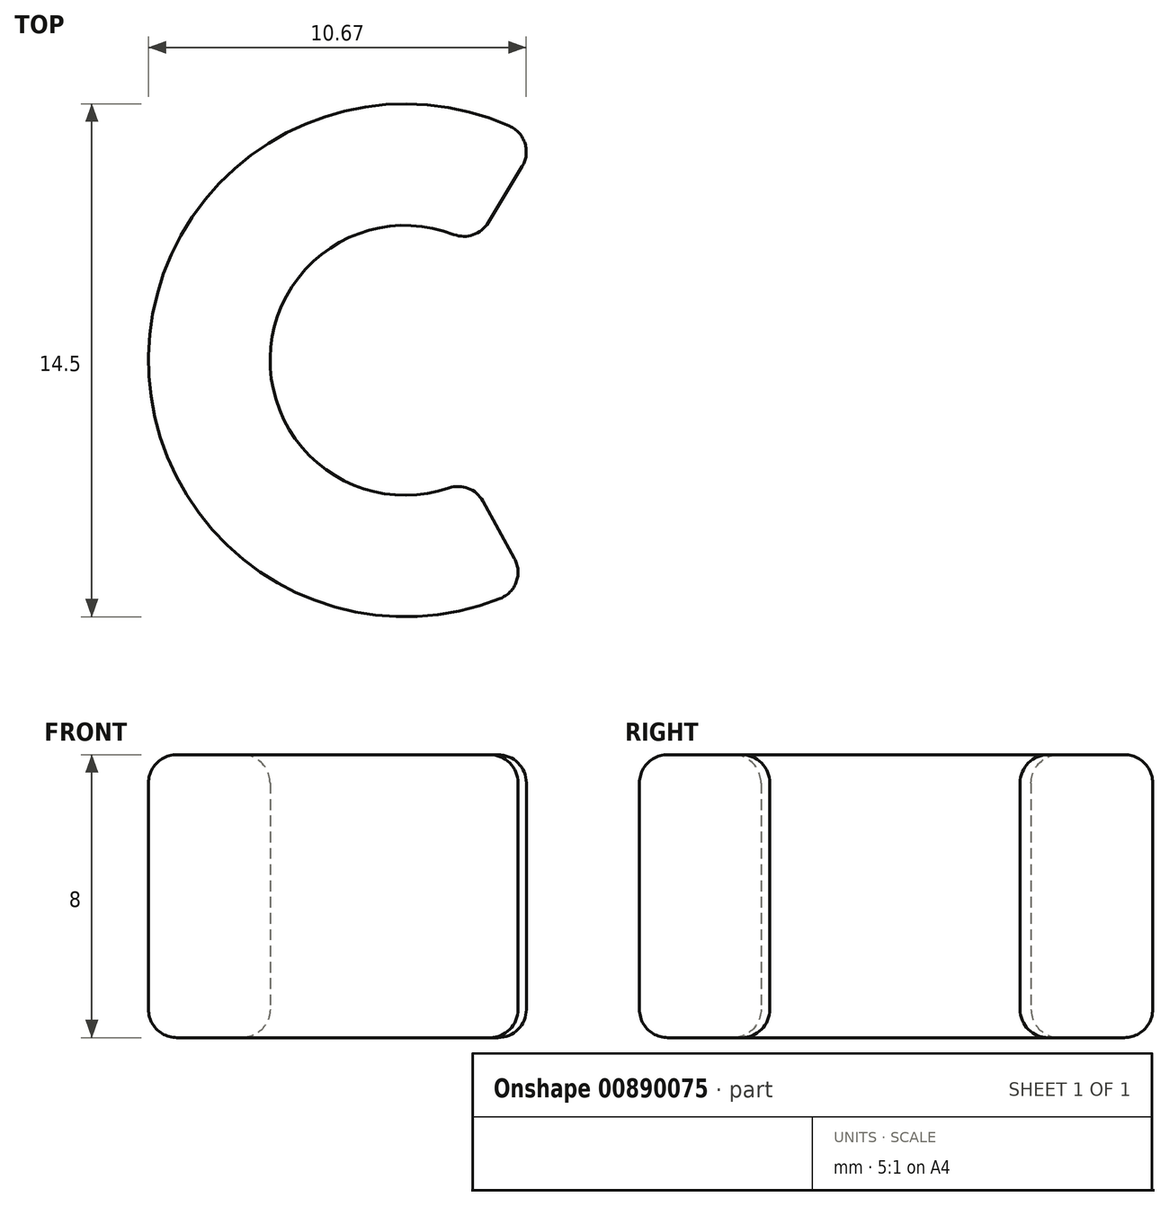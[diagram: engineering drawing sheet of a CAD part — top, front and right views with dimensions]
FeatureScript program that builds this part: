
annotation { "Feature Type Name" : "Feature", "Feature Type Description" : "" }
export const myFeature = defineFeature(function(context is Context, id is Id, definition is map)
    precondition{}
    {
        {
            var Q0;
            Q0=qCreatedBy(makeId("Top.planeOp"),FACE);
            var sketch = newSketch(context, id + "F0", { "sketchPlane" : qUnion([Q0])});
            skArc(sketch, "E0", {"start": v(1.97, 3.27) * mm, "mid": v(-3.81, 0.07) * mm, "end": v(1.84, -3.34) * mm});
            skArc(sketch, "E1", {"start": v(3.75, 6.2) * mm, "mid": v(-7.25, 0.14) * mm, "end": v(3.5, -6.35) * mm});
            skLineSegment(sketch, "E2", {"start": v(1.97, 3.27) * mm, "end": v(3.75, 6.2) * mm});
            skLineSegment(sketch, "E3", {"start": v(1.84, -3.34) * mm, "end": v(3.5, -6.35) * mm});
            skSolve(sketch);
        }
        {
            var Q0;
            Q0 = qSketchRegion(id + "F0", true);
            extrude(context, id + "F1", {"entities" : qUnion([Q0]), "flatOperationType" : FlatOperationType.REMOVE, "depth" : 8 * mm, "offsetDistance" : 25 * mm, "domain" : OperationDomain.MODEL});
        }
        {
            var Q0;
            Q0=makeQuery(id+"F1.opExtrude","CAP_EDGE",EDGE,{"disambiguationData":[OSD([sQuery(id+"F0.wireOp",EDGE,"E0")])],"isStart":false});
            var Q1;
            Q1=makeQuery(id+"F1.opExtrude","SWEPT_EDGE",EDGE,{"disambiguationData":[OSD([sQuery(id+"F0.wireOp",EDGE,"E0"),sQuery(id+"F0.wireOp",EDGE,"E2")])]});
            var Q2;
            Q2=makeQuery(id+"F1.opExtrude","CAP_EDGE",EDGE,{"disambiguationData":[OSD([sQuery(id+"F0.wireOp",EDGE,"E1")])],"isStart":false});
            var Q3;
            Q3=makeQuery(id+"F1.opExtrude","CAP_FACE",FACE,{"disambiguationData":[OSD([sQuery(id+"F0.wireOp",EDGE,"E0"),sQuery(id+"F0.wireOp",EDGE,"E1"),sQuery(id+"F0.wireOp",EDGE,"E2"),sQuery(id+"F0.wireOp",EDGE,"E3")])],"isStart":true});
            var Q4;
            Q4=makeQuery(id+"F1.opExtrude","SWEPT_FACE",FACE,{"disambiguationData":[OSD([sQuery(id+"F0.wireOp",EDGE,"E3")])]});
            var Q5;
            Q5=makeQuery(id+"F1.opExtrude","SWEPT_FACE",FACE,{"disambiguationData":[OSD([sQuery(id+"F0.wireOp",EDGE,"E2")])]});
            fillet(context, id + "F2", {"entities" : qUnion([Q0, Q1, Q2, Q3, Q4, Q5]), "radius" : 0.8 * mm, "tangentPropagation" : true, "allowEdgeOverflow" : false});
        }
    });
